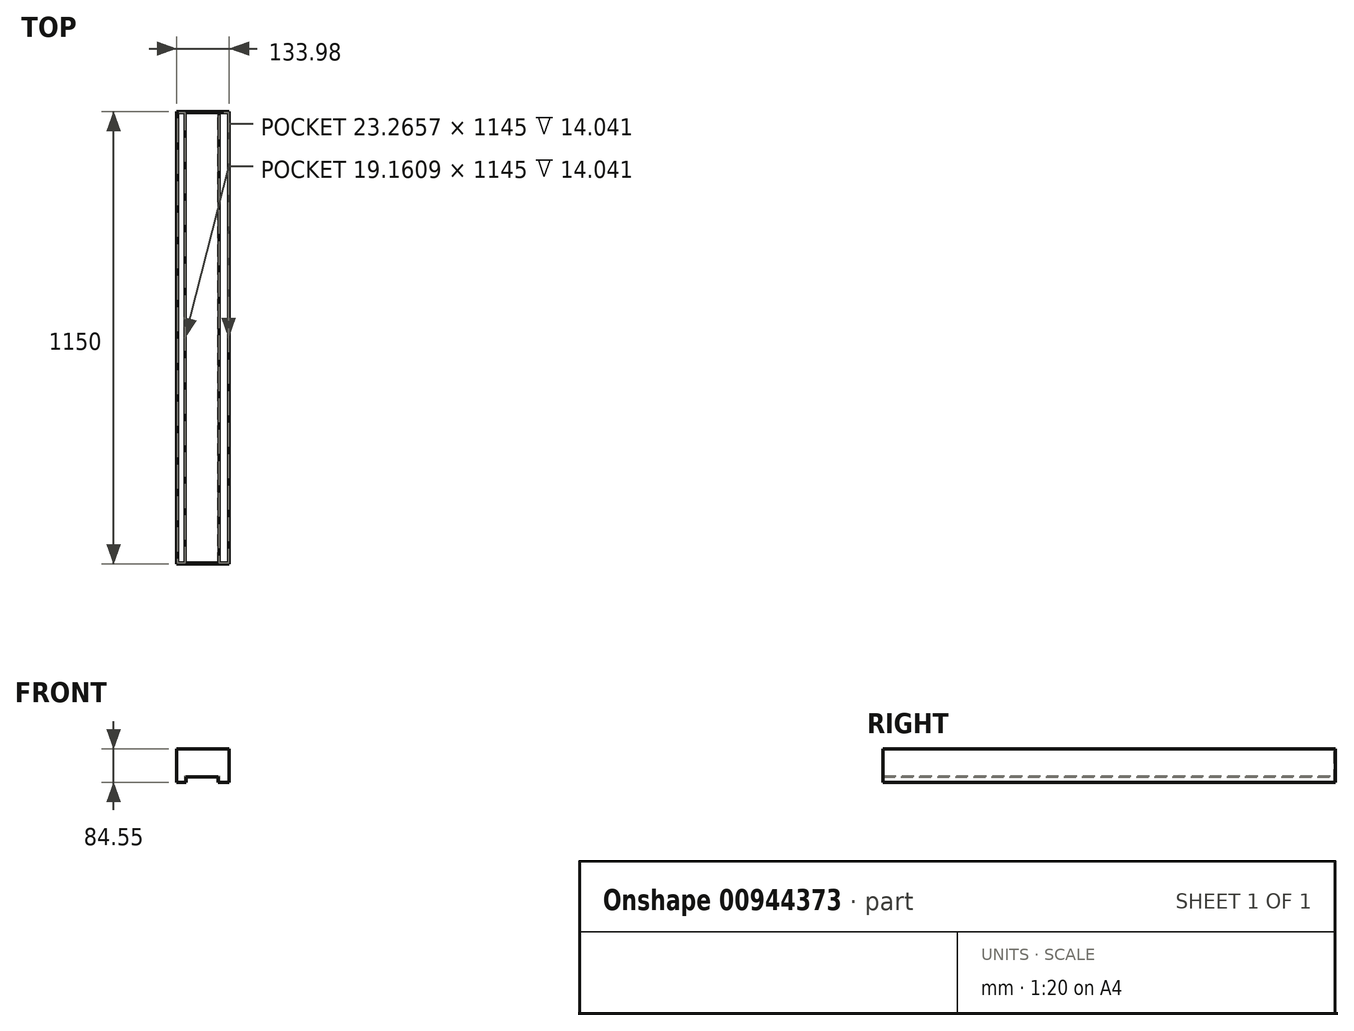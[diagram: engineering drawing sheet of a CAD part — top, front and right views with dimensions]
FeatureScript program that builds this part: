
annotation { "Feature Type Name" : "Feature", "Feature Type Description" : "" }
export const myFeature = defineFeature(function(context is Context, id is Id, definition is map)
    precondition{}
    {
        {
            var Q0;
            Q0=qCreatedBy(makeId("Front.planeOp"),FACE);
            var sketch = newSketch(context, id + "F0", { "sketchPlane" : qUnion([Q0])});
            skLineSegment(sketch, "E0", {"start": v(-49.64, 14.04) * mm, "end": v(27.81, 14.04) * mm});
            skLineSegment(sketch, "E1", {"start": v(27.81, 14.04) * mm, "end": v(84.34, 14.04) * mm});
            skLineSegment(sketch, "E2", {"start": v(84.34, 14.04) * mm, "end": v(84.34, 84.55) * mm});
            skLineSegment(sketch, "E3", {"start": v(84.34, 84.55) * mm, "end": v(-49.64, 84.55) * mm});
            skLineSegment(sketch, "E4", {"start": v(-49.64, 84.55) * mm, "end": v(-49.64, 14.04) * mm});
            skLineSegment(sketch, "E5", {"start": v(-49.64, 0) * mm, "end": v(-25.48, 0) * mm});
            skLineSegment(sketch, "E6", {"start": v(-25.48, 0) * mm, "end": v(-25.48, 14.04) * mm});
            skLineSegment(sketch, "E7", {"start": v(-49.64, 42.6) * mm, "end": v(-49.64, 14.04) * mm});
            skLineSegment(sketch, "E8", {"start": v(-49.64, 0) * mm, "end": v(-49.64, 14.04) * mm});
            skLineSegment(sketch, "E9", {"start": v(84.34, 0) * mm, "end": v(84.34, 14.04) * mm});
            skPoint(sketch, "E10.end.orphan", {"position": v(65.67, 0) * mm});
            skLineSegment(sketch, "E11", {"start": v(56.08, 0) * mm, "end": v(84.34, 0) * mm});
            skPoint(sketch, "E11.startSnap0", {"position": v(56.08, 14.04) * mm});
            skLineSegment(sketch, "E12", {"start": v(56.08, 14.04) * mm, "end": v(56.08, 0) * mm});
            skPoint(sketch, "E13.orphan", {"position": v(56.08, 46.1) * mm});
            skSolve(sketch);
        }
        {
            var Q0;
            Q0 = qSketchRegion(id + "F0", true);
            extrude(context, id + "F1", {"entities" : qUnion([Q0]), "depth" : 1150 * mm, "offsetDistance" : 25 * mm});
        }
        {
            var Q0;
            Q0=makeQuery(id+"F1.opExtrude","SWEPT_FACE",FACE,{"disambiguationData":[OSD([sQuery(id+"F0.wireOp",EDGE,"E3")])]});
            shell(context, id + "F2", {"entities" : qUnion([Q0]), "thickness" : 2.5 * mm});
        }
    });
